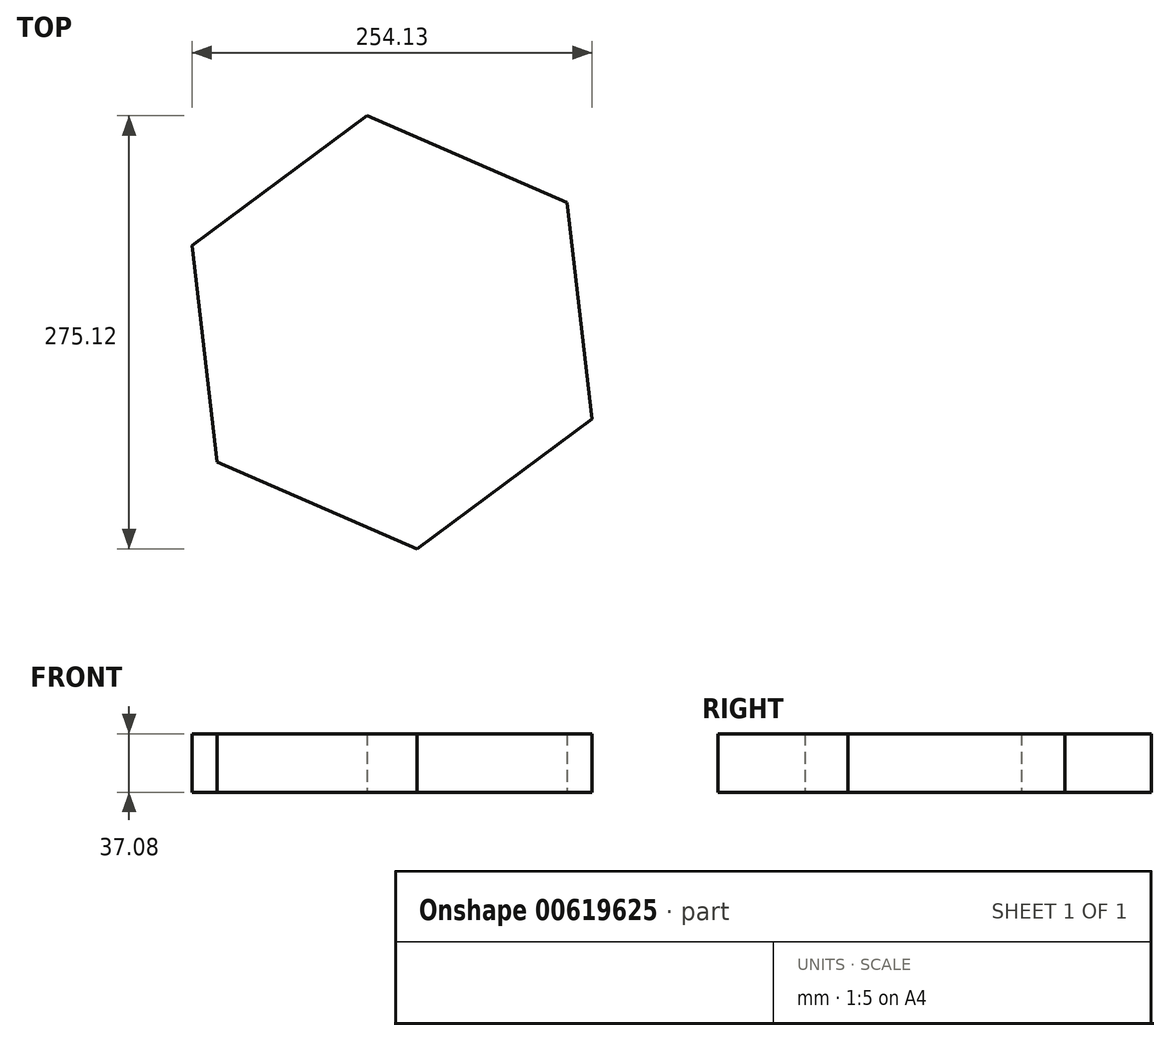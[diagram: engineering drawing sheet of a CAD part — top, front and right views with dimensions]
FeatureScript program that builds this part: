
annotation { "Feature Type Name" : "Feature", "Feature Type Description" : "" }
export const myFeature = defineFeature(function(context is Context, id is Id, definition is map)
    precondition{}
    {
        {
            var Q0;
            Q0=qCreatedBy(makeId("Top.planeOp"),FACE);
            var sketch = newSketch(context, id + "F0", { "sketchPlane" : qUnion([Q0])});
            skCircle(sketch, "E0.cCircle", {"center": v(-29.16, 0) * mm, "radius": 119.92 * mm, "construction": true});
            skLineSegment(sketch, "E0.0", {"start": v(-45.02, 137.56) * mm, "end": v(82.04, 82.52) * mm});
            skLineSegment(sketch, "E0.1", {"start": v(82.04, 82.52) * mm, "end": v(97.9, -55.04) * mm});
            skLineSegment(sketch, "E0.2", {"start": v(97.9, -55.04) * mm, "end": v(-13.29, -137.56) * mm});
            skLineSegment(sketch, "E0.3", {"start": v(-13.29, -137.56) * mm, "end": v(-140.35, -82.52) * mm});
            skLineSegment(sketch, "E0.4", {"start": v(-140.35, -82.52) * mm, "end": v(-156.22, 55.04) * mm});
            skLineSegment(sketch, "E0.5", {"start": v(-156.22, 55.04) * mm, "end": v(-45.02, 137.56) * mm});
            skPoint(sketch, "E0.0.midPoint", {"position": v(18.5, 110.04) * mm});
            skSolve(sketch);
        }
        {
            var Q0;
            Q0=makeQuery(id+"F0.imprint","IMPRINT",FACE,{"disambiguationData":[TD([[makeQuery(id+"F0.imprint","IMPRINT",EDGE,{"derivedFrom":sQuery(id+"F0.wireOp",EDGE,"E0.0")}),-1.0]])]});
            extrude(context, id + "F1", {"entities" : qUnion([Q0]), "depth" : 37.08 * mm, "offsetDistance" : 25.4 * mm});
        }
    });
